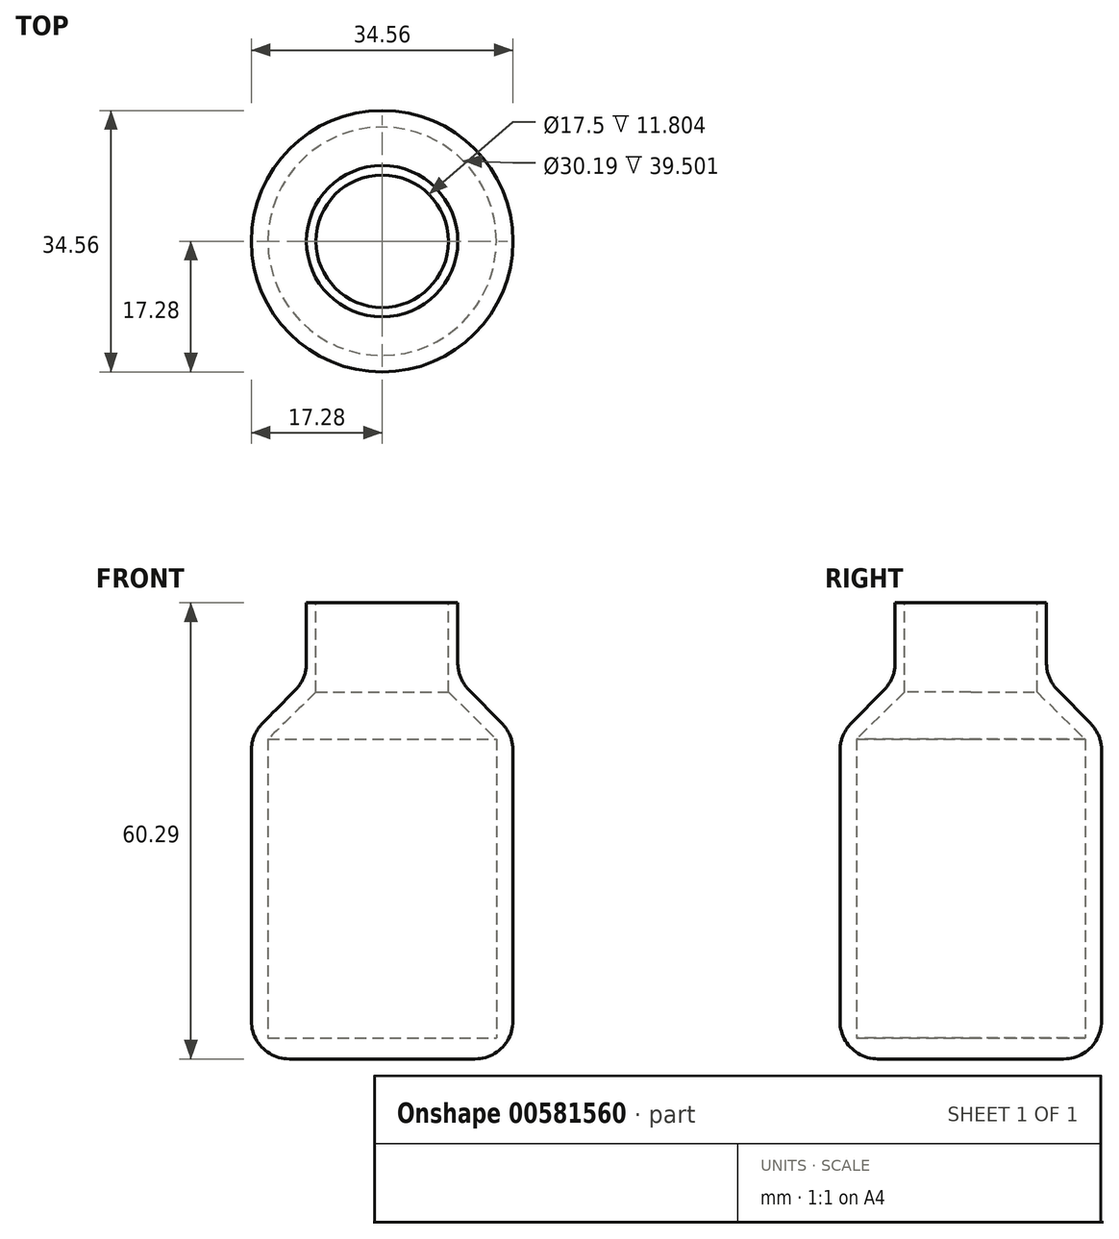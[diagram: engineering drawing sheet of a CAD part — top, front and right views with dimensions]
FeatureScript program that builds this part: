
annotation { "Feature Type Name" : "Feature", "Feature Type Description" : "" }
export const myFeature = defineFeature(function(context is Context, id is Id, definition is map)
    precondition{}
    {
        {
            var Q0;
            Q0=qCreatedBy(makeId("Right.planeOp"),FACE);
            var sketch = newSketch(context, id + "F0", { "sketchPlane" : qUnion([Q0])});
            skLineSegment(sketch, "E0", {"start": v(0, 60.29) * mm, "end": v(10, 60.29) * mm});
            skLineSegment(sketch, "E1", {"start": v(10, 60.29) * mm, "end": v(10, 50.29) * mm});
            skLineSegment(sketch, "E2", {"start": v(10, 50.29) * mm, "end": v(17.28, 42.83) * mm});
            skLineSegment(sketch, "E3", {"start": v(17.28, 42.83) * mm, "end": v(17.28, 0) * mm});
            skLineSegment(sketch, "E4", {"start": v(17.28, 0) * mm, "end": v(0, 0) * mm});
            skLineSegment(sketch, "E5", {"start": v(0, 0) * mm, "end": v(0, 2.78) * mm});
            skLineSegment(sketch, "E6", {"start": v(0, 2.78) * mm, "end": v(15.1, 2.78) * mm});
            skLineSegment(sketch, "E7", {"start": v(15.1, 2.78) * mm, "end": v(15.1, 42.28) * mm});
            skLineSegment(sketch, "E8", {"start": v(15.1, 42.28) * mm, "end": v(6.9, 50.29) * mm});
            skLineSegment(sketch, "E9", {"start": v(6.9, 50.29) * mm, "end": v(6.9, 57.74) * mm});
            skLineSegment(sketch, "E10", {"start": v(6.9, 57.74) * mm, "end": v(0, 57.74) * mm});
            skLineSegment(sketch, "E11", {"start": v(0, 57.74) * mm, "end": v(0, 60.29) * mm});
            skSolve(sketch);
        }
        {
            var Q0;
            Q0=makeQuery(id+"F0.imprint","IMPRINT",FACE,{"disambiguationData":[TD([[makeQuery(id+"F0.imprint","IMPRINT",EDGE,{"derivedFrom":sQuery(id+"F0.wireOp",EDGE,"E0")}),-1.0]])]});
            var sketch = newSketch(context, id + "F1", { "sketchPlane" : qUnion([Q0])});
            skLineSegment(sketch, "E12", {"start": v(0, 57.77) * mm, "end": v(0, 0) * mm});
            skLineSegment(sketch, "E13", {"start": v(0, 0) * mm, "end": v(0, 60.74) * mm});
            skSolve(sketch);
        }
        {
            var Q0;
            Q0=makeQuery(id+"F0.imprint","IMPRINT",FACE,{"disambiguationData":[TD([[makeQuery(id+"F0.imprint","IMPRINT",EDGE,{"derivedFrom":sQuery(id+"F0.wireOp",EDGE,"E0")}),-1.0]])]});
            var Q1;
            Q1=sQuery(id+"F1.wireOp",EDGE,"E13");
            revolve(context, id + "F2", {"entities" : qUnion([Q0]), "axis" : qUnion([Q1]), "revolveType" : RevolveType.FULL});
        }
        {
            var Q0;
            Q0=makeQuery(id+"F2.opRevolve","SWEPT_FACE",FACE,{"disambiguationData":[OSD([sQuery(id+"F0.wireOp",EDGE,"E0")])]});
            var sketch = newSketch(context, id + "F3", { "sketchPlane" : qUnion([Q0])});
            skCircle(sketch, "E14", {"center": v(0, 0) * mm, "radius": 8.75 * mm});
            skSolve(sketch);
        }
        {
            var Q0;
            Q0=makeQuery(id+"F3.imprint","IMPRINT",FACE,{"disambiguationData":[TD([[makeQuery(id+"F3.imprint","IMPRINT",EDGE,{"derivedFrom":sQuery(id+"F3.wireOp",EDGE,"E14")}),1.0]])]});
            extrude(context, id + "F4", {"entities" : qUnion([Q0]), "operationType" : NewBodyOperationType.REMOVE, "oppositeDirection" : true, "depth" : 25 * mm, "offsetDistance" : 25 * mm});
        }
        {
            var Q0;
            Q0=makeQuery(id+"F2.opRevolve","SWEPT_EDGE",EDGE,{"disambiguationData":[OSD([sQuery(id+"F0.wireOp",EDGE,"E1"),sQuery(id+"F0.wireOp",EDGE,"E2")])]});
            var Q1;
            Q1=makeQuery(id+"F2.opRevolve","SWEPT_EDGE",EDGE,{"disambiguationData":[OSD([sQuery(id+"F0.wireOp",EDGE,"E2"),sQuery(id+"F0.wireOp",EDGE,"E3")])]});
            var Q2;
            Q2=makeQuery(id+"F2.opRevolve","SWEPT_EDGE",EDGE,{"disambiguationData":[OSD([sQuery(id+"F0.wireOp",EDGE,"E3"),sQuery(id+"F0.wireOp",EDGE,"E4")])]});
            fillet(context, id + "F5", {"entities" : qUnion([Q0, Q1, Q2]), "radius" : 5 * mm, "tangentPropagation" : true, "allowEdgeOverflow" : false});
        }
    });
